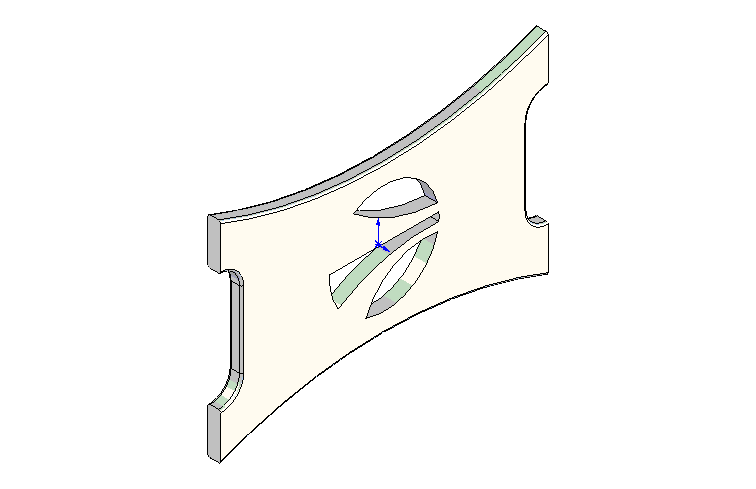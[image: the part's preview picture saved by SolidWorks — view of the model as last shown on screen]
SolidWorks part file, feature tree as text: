
SOLIDWORKS PART (.sldprt)
format: sldprt  version: not decoded by parser v0  size: 382,464 bytes
history: native  units: mm
features: plane x3, sketch x3, cut_extrude x2, material x1, extrude x1, fillet x1 (+10 scaffold rows collapsed)
feature tree (21):
  scaffold x10  (default folders/planes/origin — collapsed)
  material  "Matériau <non spécifié>"
  plane  "Plan de face"
  plane  "Plan de dessus"
  plane  "Plan de droite"
  sketch  "Esquisse1"  dims[c1.D2=8.5mm c1.D3=8.5mm c1.D1=3.0mm c2.D3=94.5mm]
  extrude  "Extrusion1"  Depth=50mm
  sketch  "Esquisse2"  dims[D1=35.0mm D2=5.0mm D3=28.0mm]
  cut_extrude  "Enlèv. mat.-Extru.1"  [1 undecoded]
  sketch  "Esquisse3"  dims[c1.D1=26.0mm c1.D6=35.0mm c1.D9=15.0mm c1.D11=40.0mm c1.D2=1.0mm c1.D3=2.0mm c2.D2=1.0mm c2.D4=3.0mm c2.D5=20.0mm c2.D6=~16.011345mm c2.D7=17.0mm c2.D8=3.0mm c2.D10=8.0mm]
  cut_extrude  "Enlèv. mat.-Extru.2"  [1 undecoded]
  fillet  "Congé1"  Radius=0.5mm
decode coverage: 5 of 7 modeling features carry decoded parameters
note: ~ marks probable driven/reference dimensions
note: 2 parameter values undecoded
note: suppression state not decoded; provenance and decode notes live in map.json
